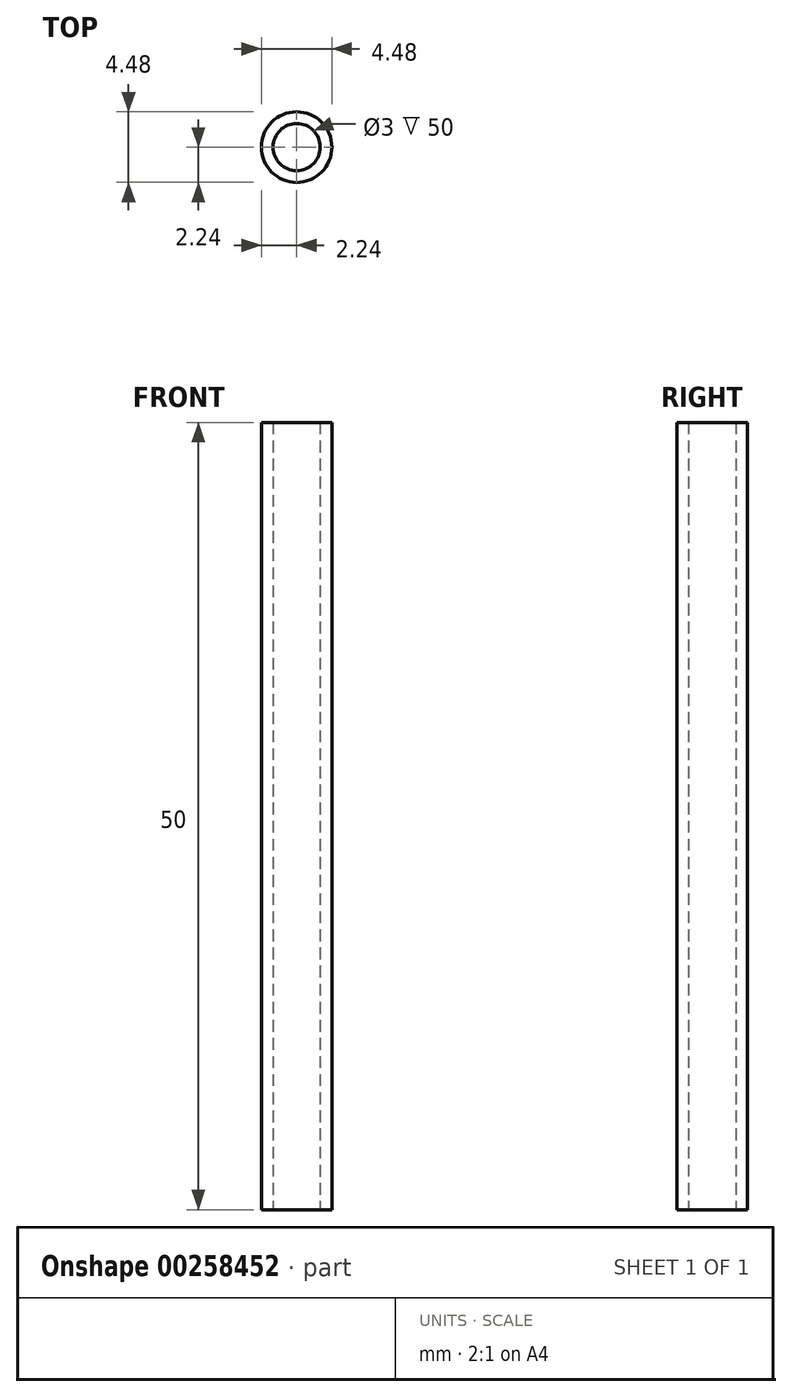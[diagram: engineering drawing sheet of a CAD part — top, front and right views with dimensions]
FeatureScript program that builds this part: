
annotation { "Feature Type Name" : "Feature", "Feature Type Description" : "" }
export const myFeature = defineFeature(function(context is Context, id is Id, definition is map)
    precondition{}
    {
        {
            var Q0;
            Q0=qCreatedBy(makeId("Top.planeOp"),FACE);
            var sketch = newSketch(context, id + "F0", { "sketchPlane" : qUnion([Q0])});
            skCircle(sketch, "E0", {"center": v(0, 0) * mm, "radius": 2.24 * mm});
            skCircle(sketch, "E1", {"center": v(0, 0) * mm, "radius": 1.5 * mm});
            skSolve(sketch);
        }
        {
            var Q0;
            Q0=makeQuery(id+"F0.imprint","IMPRINT",FACE,{"disambiguationData":[TD([[makeQuery(id+"F0.imprint","IMPRINT",EDGE,{"derivedFrom":sQuery(id+"F0.wireOp",EDGE,"E0")}),1.0]])]});
            extrude(context, id + "F1", {"entities" : qUnion([Q0]), "depth" : 50 * mm});
        }
    });
